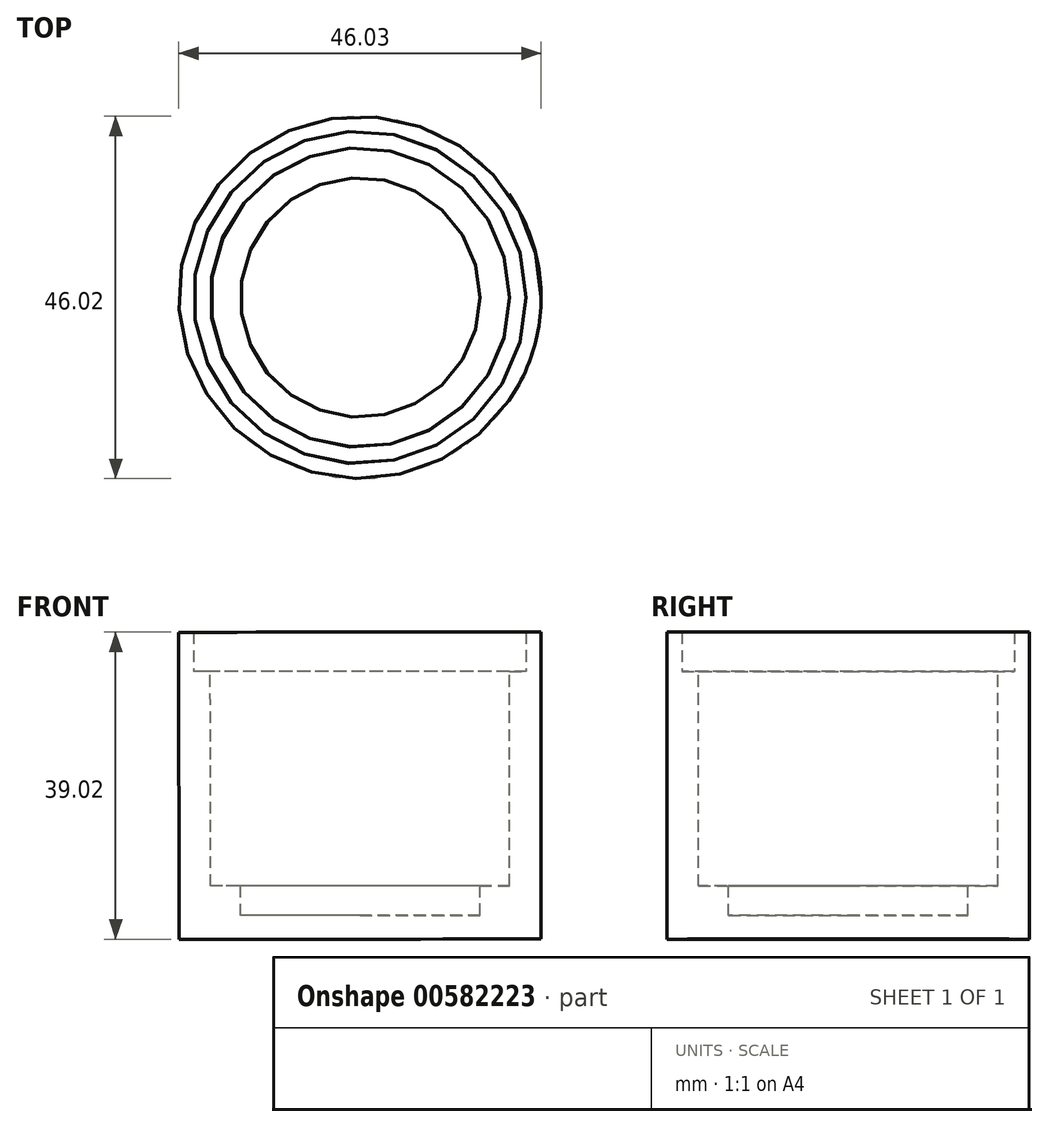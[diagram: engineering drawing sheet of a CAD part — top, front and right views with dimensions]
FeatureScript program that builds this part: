
annotation { "Feature Type Name" : "Feature", "Feature Type Description" : "" }
export const myFeature = defineFeature(function(context is Context, id is Id, definition is map)
    precondition{}
    {
        {
            var Q0;
            Q0=qCreatedBy(makeId("Front.planeOp"),FACE);
            var sketch = newSketch(context, id + "F0", { "sketchPlane" : qUnion([Q0])});
            skLineSegment(sketch, "E0", {"start": v(-20.9, 27.24) * mm, "end": v(-20.9, 32.25) * mm});
            skLineSegment(sketch, "E1", {"start": v(-20.9, 32.25) * mm, "end": v(-22.8, 32.25) * mm});
            skLineSegment(sketch, "E2", {"start": v(-20.9, 27.24) * mm, "end": v(-18.8, 27.25) * mm});
            skLineSegment(sketch, "E3", {"start": v(-22.8, 32.25) * mm, "end": v(-22.77, -6.75) * mm});
            skLineSegment(sketch, "E4", {"start": v(0.23, -3.74) * mm, "end": v(0.23, -6.73) * mm});
            skLineSegment(sketch, "E5", {"start": v(-22.77, -6.75) * mm, "end": v(0.23, -6.73) * mm});
            skLineSegment(sketch, "E6.MirrorCS", {"start": v(21.33, 32.27) * mm, "end": v(23.23, 32.27) * mm});
            skLineSegment(sketch, "E7.MirrorCS", {"start": v(21.33, 27.26) * mm, "end": v(21.33, 32.27) * mm});
            skLineSegment(sketch, "E8.MirrorCS", {"start": v(21.33, 27.26) * mm, "end": v(19.23, 27.26) * mm});
            skLineSegment(sketch, "E9.MirrorCS", {"start": v(23.23, 32.27) * mm, "end": v(23.23, -6.73) * mm});
            skLineSegment(sketch, "E10.MirrorCS", {"start": v(23.23, -6.73) * mm, "end": v(0.23, -6.73) * mm});
            skLineSegment(sketch, "E11.top", {"start": v(-18.77, 0) * mm, "end": v(-14.97, 0) * mm});
            skLineSegment(sketch, "E11.right", {"start": v(-14.97, -3.74) * mm, "end": v(-14.97, 0) * mm});
            skLineSegment(sketch, "E12", {"start": v(-14.97, -3.74) * mm, "end": v(0.23, -3.74) * mm});
            skLineSegment(sketch, "E13", {"start": v(-18.77, 0) * mm, "end": v(-18.8, 27.25) * mm});
            skLineSegment(sketch, "E14.MirrorCS", {"start": v(15.43, -3.73) * mm, "end": v(15.43, 0.01) * mm});
            skLineSegment(sketch, "E15.MirrorCS", {"start": v(19.23, 0.02) * mm, "end": v(15.43, 0.01) * mm});
            skLineSegment(sketch, "E16.MirrorCS", {"start": v(19.23, 0.02) * mm, "end": v(19.23, 27.26) * mm});
            skLineSegment(sketch, "E17.MirrorCS", {"start": v(15.43, -3.73) * mm, "end": v(0.23, -3.74) * mm});
            skSolve(sketch);
        }
        {
            var Q0;
            Q0=makeQuery(id+"F0.imprint","IMPRINT",FACE,{"disambiguationData":[TD([[makeQuery(id+"F0.imprint","IMPRINT",EDGE,{"derivedFrom":sQuery(id+"F0.wireOp",EDGE,"E0")}),1.0]])]});
            var Q1;
            Q1=sQuery(id+"F0.wireOp",EDGE,"E4");
            revolve(context, id + "F1", {"entities" : qUnion([Q0]), "axis" : qUnion([Q1]), "revolveType" : RevolveType.FULL});
        }
    });
